# Revit family: IS_Conca_A7374_BIM_GB
name_source: partatom
category: Plumbing Fixtures
revit_build: Autodesk Revit 2017 (Build: 20160225_1515(x64)
units: mm (PartAtom-declared; Revit-internal decimal feet)

## family parameters
Always vertical = No
Cut with Voids When Loaded = No
OmniClass Number = 23.45.55.17
OmniClass Title = Mixing Faucets
Part Type = Normal
Room Calculation Point = No
Round Connector Dimension = Use Diameter
Shared = No
Work Plane-Based = No

## types (4) — shared parameters
Accessories = https://www.idealspec.co.uk
AreaUnits = millimeters
AssetType = Fixed
BIMobject category = Sanitary: Taps & Mixer
BarCode = 3800861085775
Brand = Ideal Standard
Brand url = http://www.idealstandard.co.uk
ConnectionType = Plumbing
CurrencyUnit = £
CurrentRevision = 1
Date of publishing = 22/09/2020
Edition number = 1
ExpectedLife = 30
FaucetFunction = UNSET
FaucetOperation = OTHER
FaucetType = OTHER
FlushRate = 0.00 m³
GTIN code = https://3800861085775
Help = https://www.idealspec.co.uk
IFC Classification = Sanitary Terminal
IfcExportAs = IfcValveType
IfcExportType = FAUCET
Installation instructions = https://www.idealspec.co.uk
InstallationInstructions = https://www.idealspec.co.uk
IsBuiltIn = No
IsHighPressure = No
IsSingleFlush = No
LinearUnits = millimeters
MaintenanceInformation = https://www.idealspec.co.uk
Manufacturer = Ideal Standard (UK) Ltd
Manufacturer name = Ideal Standard
ManufacturerURL = https://www.idealspec.co.uk
Material = Brass
Material main = Brass
Product Guid = dc78788c-54c9-42e4-9303-507d6a86c945
Product SKU = A7374
Product certification = https://www.idealspec.co.uk
Product data url = https://bimobject.com
Product family = Conca
Product group = BATH-SHOWER MIXERS
Product name = CONCA BSH MXR BIN KIT2/EASY-BOX BR GUNM
Product url = https://www.idealstandard.co.uk
ProductInformation = https://www.idealspec.co.uk
QR code = http://bimobject.com
Shape = Cylindrical
Size = 163 x 82 x 197 mm
Space = Internal
SpareParts = https://fastpart-spares.co.uk
Technical description = https://www.idealspec.co.uk
TestPressure = 10 Bar
UNSPSC Code = 301815
URL = https://www.idealspec.co.uk
Uniclass 1.4 Code = L725111
Uniclass 1.4 Description = Mixer taps
Uniclass2015Version = v1.1
Version = 1
VolumeUnits = Litres
WRASURL = https://www.wras.co.uk
WarrantyDescription = Manufacturers Warranty
WarrantyDurationParts = 5
WarrantyDurationUnit = year
WarrantyGuarantorParts = https://www.idealspec.co.uk
zero-valued in all types: FlushingRate, InletConnectionSize, MaterialThickness, OutletConnectionSize

## per-type parameters (varying)
- A7374AA - CONCA BSH MXR BIN KIT2/EASY-BOX CHR: BIMObjectName=IS_IdealStandard_BathTaps_Conca_A7374; Color=Chrome; Description=Conca Single Lever built in bath shower mixer - Requires built in kit A1000NU and a suitable outlet.; Features=Single lever built in bath shower mixer - Requires built in kit A1000NU and a suitable outlet.; Finish=Chrome; MainColor=Chrome; Model=A7374AA; ModelNumber=A7374AA; ModelReference=Single lever built in bath shower mixer - Requires built in kit A1000NU and a suitable outlet.; NBS Reference Code=45-35-70/315; NBS Reference Description=Water supply fittings for baths; Name=BathTaps_Conca_A7374_IdealStandard; NettWeight=1,45 KG; NominalDepth=82 mm; NominalHeight=197 mm; NominalLength=82 mm; NominalWidth=163 mm  [stored 0.534777 ft]; Uniclass 2.0 Code=Pr_40_30_96_09; Uniclass 2.0 Description=Bath Taps; Uniclass 2015 Code=Pr_40_20_87_09; Uniclass 2015 Name=Bath taps; Uniclass2015Code=Pr_40_20_87_09; Uniclass2015Title=Bath taps; Uniformat II Code=Pr_40_30_96_09; Uniformat II Description=Bath Taps
- A7374A2 - CONCA BSH MXR BIN KIT2/EASY-BOX BR GOLD: BIMObjectName=IS_IdealStandard_ShowerManualWaterSupplySets_Conca_A7374; Color=Brushed gold; Description=Conca Single Lever built in shower mixer - Requires built in kit A1000NU and a suitable outlet.; Features=Single lever built in shower mixer - Requires built in kit A1000NU and a suitable outlet.; Finish=Brushed gold; MainColor=Brushed gold; Model=A7374A2; ModelNumber=A7374A2; ModelReference=Single lever built in shower mixer - Requires built in kit A1000NU and a suitable outlet.; NBS Reference Code=45-35-70/335; NBS Reference Description=Shower mixers; Name=ShowerManualWaterSupplySets_Conca_A7374_IdealStandard; NettWeight=L725111; NominalDepth=180 mm  [stored 0.590551 ft]; NominalHeight=215 mm; NominalLength=180 mm  [stored 0.590551 ft]; NominalWidth=172 mm  [stored 0.564304 ft]; OmniClass Description=Pr_40_20_87_78; Uniclass 2.0 Code=Pr_40_30_96_78; Uniclass 2.0 Description=Shower Manual Water Supply Sets; Uniclass 2015 Code=Pr_40_20_87_78; Uniclass 2015 Name=Shower manual water supply sets; Uniclass2015Code=Pr_40_20_87_78; Uniclass2015Title=Shower manual water supply sets; Uniformat II Code=Pr_40_30_96_78; Uniformat II Description=Shower Manual Water Supply Sets
- A7374A5 - CONCA BSH MXR BIN KIT2/EASY-BOX MGN GREY: BIMObjectName=IS_IdealStandard_ShowerManualWaterSupplySets_Conca_A7374; Color=Brushed Gun metal; Description=Conca Single Lever built in shower mixer - Requires built in kit A1000NU and a suitable outlet.; Features=Single lever built in shower mixer - Requires built in kit A1000NU and a suitable outlet.; Finish=Brushed Gun metal; MainColor=Brushed Gun metal; Model=A7374A5; ModelNumber=A7374A5; ModelReference=Single lever built in shower mixer - Requires built in kit A1000NU and a suitable outlet.; NBS Reference Code=45-35-70/335; NBS Reference Description=Shower mixers; Name=ShowerManualWaterSupplySets_Conca_A7374_IdealStandard; NettWeight=L725111; NominalDepth=180 mm  [stored 0.590551 ft]; NominalHeight=215 mm; NominalLength=180 mm  [stored 0.590551 ft]; NominalWidth=172 mm  [stored 0.564304 ft]; OmniClass Description=Pr_40_20_87_78; Uniclass 2.0 Code=Pr_40_30_96_78; Uniclass 2.0 Description=Shower Manual Water Supply Sets; Uniclass 2015 Code=Pr_40_20_87_78; Uniclass 2015 Name=Shower manual water supply sets; Uniclass2015Code=Pr_40_20_87_78; Uniclass2015Title=Shower manual water supply sets; Uniformat II Code=Pr_40_30_96_78; Uniformat II Description=Shower Manual Water Supply Sets
- A7374GN - CONCA BSH MXR BIN KIT2/EASY-BOX SILV STO: BIMObjectName=IS_IdealStandard_ShowerManualWaterSupplySets_Conca_A7374; Color=Brushed nickel; Description=Conca Single Lever built in shower mixer - Requires built in kit A1000NU and a suitable outlet.; Features=Single lever built in shower mixer - Requires built in kit A1000NU and a suitable outlet.; Finish=Brushed nickel; MainColor=Brushed nickel; Model=A7374GN; ModelNumber=A7374GN; ModelReference=Single lever built in shower mixer - Requires built in kit A1000NU and a suitable outlet.; NBS Reference Code=45-35-70/335; NBS Reference Description=Shower mixers; Name=ShowerManualWaterSupplySets_Conca_A7374_IdealStandard; NettWeight=L725111; NominalDepth=180 mm  [stored 0.590551 ft]; NominalHeight=215 mm; NominalLength=180 mm  [stored 0.590551 ft]; NominalWidth=172 mm  [stored 0.564304 ft]; OmniClass Description=Pr_40_20_87_78; Uniclass 2.0 Code=Pr_40_30_96_78; Uniclass 2.0 Description=Shower Manual Water Supply Sets; Uniclass 2015 Code=Pr_40_20_87_78; Uniclass 2015 Name=Shower manual water supply sets; Uniclass2015Code=Pr_40_20_87_78; Uniclass2015Title=Shower manual water supply sets; Uniformat II Code=Pr_40_30_96_78; Uniformat II Description=Shower Manual Water Supply Sets

note: [stored X ft] marks values corroborated as IEEE doubles in the binary element streams (Revit-internal decimal feet)

## geometry (parser evidence)
native form markers: Sweep x3
no freeform markers — native parametric forms only
